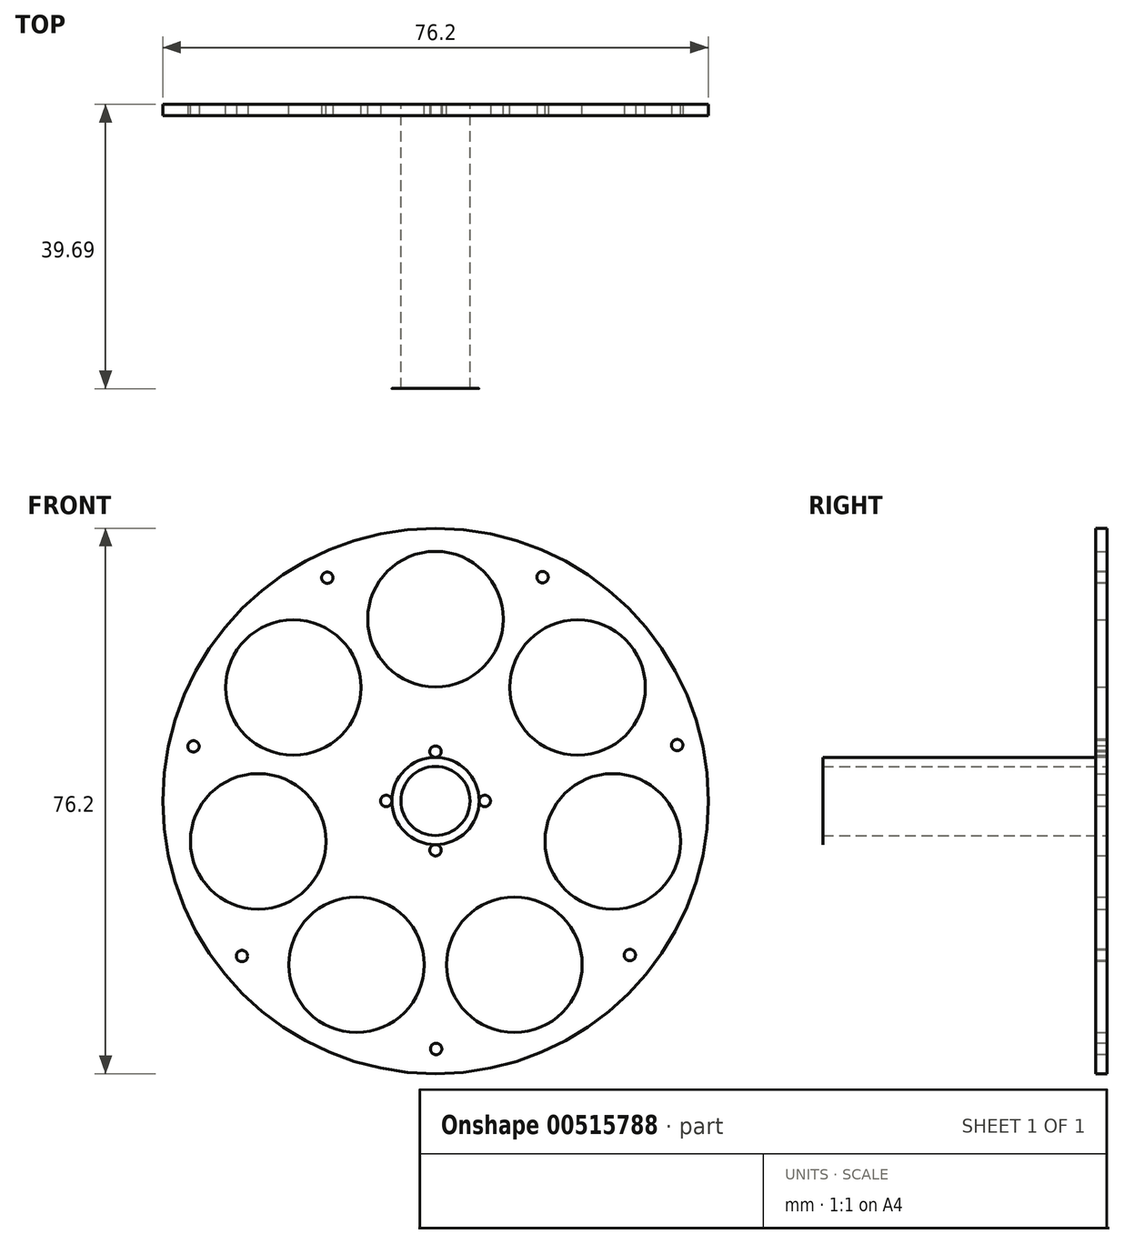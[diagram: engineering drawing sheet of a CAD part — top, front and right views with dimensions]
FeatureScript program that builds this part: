
annotation { "Feature Type Name" : "Feature", "Feature Type Description" : "" }
export const myFeature = defineFeature(function(context is Context, id is Id, definition is map)
    precondition{}
    {
        {
            var Q0;
            Q0=qCreatedBy(makeId("Front.planeOp"),FACE);
            var sketch = newSketch(context, id + "F0", { "sketchPlane" : qUnion([Q0])});
            skCircle(sketch, "E0", {"center": v(0, 0) * mm, "radius": 38.1 * mm});
            skCircle(sketch, "E1", {"center": v(0, 25.4) * mm, "radius": 9.46 * mm});
            skCircle(sketch, "E2.1.0", {"center": v(-19.86, 15.84) * mm, "radius": 9.46 * mm});
            skCircle(sketch, "E2.2.0", {"center": v(-24.76, -5.65) * mm, "radius": 9.46 * mm});
            skCircle(sketch, "E2.3.0", {"center": v(-11.02, -22.88) * mm, "radius": 9.46 * mm});
            skCircle(sketch, "E2.4.0", {"center": v(11.02, -22.88) * mm, "radius": 9.46 * mm});
            skCircle(sketch, "E2.5.0", {"center": v(24.76, -5.65) * mm, "radius": 9.46 * mm});
            skCircle(sketch, "E2.6.0", {"center": v(19.86, 15.84) * mm, "radius": 9.46 * mm});
            skCircle(sketch, "E3", {"center": v(0, 0) * mm, "radius": 4.83 * mm});
            skSolve(sketch);
        }
        {
            var Q0;
            Q0=makeQuery(id+"F0.imprint","IMPRINT",FACE,{"disambiguationData":[TD([[makeQuery(id+"F0.imprint","IMPRINT",EDGE,{"derivedFrom":sQuery(id+"F0.wireOp",EDGE,"E0")}),1.0]])]});
            extrude(context, id + "F1", {"entities" : qUnion([Q0]), "depth" : 1.59 * mm, "offsetDistance" : 25.4 * mm});
        }
        {
            var Q0;
            Q0=makeQuery(id+"F1.opExtrude","CAP_FACE",FACE,{"disambiguationData":[OSD([sQuery(id+"F0.wireOp",EDGE,"E0"),sQuery(id+"F0.wireOp",EDGE,"E1"),sQuery(id+"F0.wireOp",EDGE,"E2.1.0"),sQuery(id+"F0.wireOp",EDGE,"E2.2.0"),sQuery(id+"F0.wireOp",EDGE,"E2.3.0"),sQuery(id+"F0.wireOp",EDGE,"E2.4.0"),sQuery(id+"F0.wireOp",EDGE,"E2.5.0"),sQuery(id+"F0.wireOp",EDGE,"E2.6.0"),sQuery(id+"F0.wireOp",EDGE,"E3")])],"isStart":false});
            var sketch = newSketch(context, id + "F2", { "sketchPlane" : qUnion([Q0])});
            skCircle(sketch, "E4", {"center": v(0, 0) * mm, "radius": 4.83 * mm});
            skCircle(sketch, "E5", {"center": v(0, 0) * mm, "radius": 6.1 * mm});
            skSolve(sketch);
        }
        {
            var Q0;
            Q0=makeQuery(id+"F2.imprint","IMPRINT",FACE,{"disambiguationData":[TD([[makeQuery(id+"F2.imprint","IMPRINT",EDGE,{"derivedFrom":sQuery(id+"F2.wireOp",EDGE,"E4")}),-1.0]])]});
            extrude(context, id + "F3", {"entities" : qUnion([Q0]), "operationType" : NewBodyOperationType.ADD, "depth" : 38.1 * mm, "offsetDistance" : 25.4 * mm});
        }
        {
            var Q0;
            Q0=makeQuery(id+"F1.opExtrude","CAP_FACE",FACE,{"disambiguationData":[OSD([sQuery(id+"F0.wireOp",EDGE,"E0"),sQuery(id+"F0.wireOp",EDGE,"E1"),sQuery(id+"F0.wireOp",EDGE,"E2.1.0"),sQuery(id+"F0.wireOp",EDGE,"E2.2.0"),sQuery(id+"F0.wireOp",EDGE,"E2.3.0"),sQuery(id+"F0.wireOp",EDGE,"E2.4.0"),sQuery(id+"F0.wireOp",EDGE,"E2.5.0"),sQuery(id+"F0.wireOp",EDGE,"E2.6.0"),sQuery(id+"F0.wireOp",EDGE,"E3")])],"isStart":false});
            var sketch = newSketch(context, id + "F4", { "sketchPlane" : qUnion([Q0])});
            skCircle(sketch, "E6", {"center": v(6.89, 0) * mm, "radius": 0.8 * mm});
            skCircle(sketch, "E7.1.0", {"center": v(0, 6.89) * mm, "radius": 0.8 * mm});
            skCircle(sketch, "E7.2.0", {"center": v(-6.89, 0) * mm, "radius": 0.8 * mm});
            skCircle(sketch, "E7.3.0", {"center": v(0, -6.89) * mm, "radius": 0.8 * mm});
            skPoint(sketch, "E7.center", {"position": v(0, 0) * mm});
            skCircle(sketch, "E8", {"center": v(33.76, 7.8) * mm, "radius": 0.8 * mm});
            skCircle(sketch, "E9.1.0", {"center": v(14.95, 31.26) * mm, "radius": 0.8 * mm});
            skCircle(sketch, "E9.2.0", {"center": v(-15.12, 31.18) * mm, "radius": 0.8 * mm});
            skCircle(sketch, "E9.3.0", {"center": v(-33.8, 7.62) * mm, "radius": 0.8 * mm});
            skCircle(sketch, "E9.4.0", {"center": v(-27.03, -21.67) * mm, "radius": 0.8 * mm});
            skCircle(sketch, "E9.5.0", {"center": v(0.09, -34.65) * mm, "radius": 0.8 * mm});
            skCircle(sketch, "E9.6.0", {"center": v(27.15, -21.53) * mm, "radius": 0.8 * mm});
            skSolve(sketch);
        }
        {
            var Q0;
            Q0=makeQuery(id+"F4.imprint","IMPRINT",FACE,{"disambiguationData":[TD([[makeQuery(id+"F4.imprint","IMPRINT",EDGE,{"derivedFrom":sQuery(id+"F4.wireOp",EDGE,"E7.3.0")}),1.0]])]});
            var Q1;
            Q1=makeQuery(id+"F4.imprint","IMPRINT",FACE,{"disambiguationData":[TD([[makeQuery(id+"F4.imprint","IMPRINT",EDGE,{"derivedFrom":sQuery(id+"F4.wireOp",EDGE,"E6")}),1.0]])]});
            var Q2;
            Q2=makeQuery(id+"F4.imprint","IMPRINT",FACE,{"disambiguationData":[TD([[makeQuery(id+"F4.imprint","IMPRINT",EDGE,{"derivedFrom":sQuery(id+"F4.wireOp",EDGE,"E9.6.0")}),1.0]])]});
            var Q3;
            Q3=makeQuery(id+"F4.imprint","IMPRINT",FACE,{"disambiguationData":[TD([[makeQuery(id+"F4.imprint","IMPRINT",EDGE,{"derivedFrom":sQuery(id+"F4.wireOp",EDGE,"E8")}),1.0]])]});
            var Q4;
            Q4=makeQuery(id+"F4.imprint","IMPRINT",FACE,{"disambiguationData":[TD([[makeQuery(id+"F4.imprint","IMPRINT",EDGE,{"derivedFrom":sQuery(id+"F4.wireOp",EDGE,"E9.5.0")}),1.0]])]});
            var Q5;
            Q5=makeQuery(id+"F4.imprint","IMPRINT",FACE,{"disambiguationData":[TD([[makeQuery(id+"F4.imprint","IMPRINT",EDGE,{"derivedFrom":sQuery(id+"F4.wireOp",EDGE,"E9.4.0")}),1.0]])]});
            var Q6;
            Q6=makeQuery(id+"F4.imprint","IMPRINT",FACE,{"disambiguationData":[TD([[makeQuery(id+"F4.imprint","IMPRINT",EDGE,{"derivedFrom":sQuery(id+"F4.wireOp",EDGE,"E9.3.0")}),1.0]])]});
            var Q7;
            Q7=makeQuery(id+"F4.imprint","IMPRINT",FACE,{"disambiguationData":[TD([[makeQuery(id+"F4.imprint","IMPRINT",EDGE,{"derivedFrom":sQuery(id+"F4.wireOp",EDGE,"E9.2.0")}),1.0]])]});
            var Q8;
            Q8=makeQuery(id+"F4.imprint","IMPRINT",FACE,{"disambiguationData":[TD([[makeQuery(id+"F4.imprint","IMPRINT",EDGE,{"derivedFrom":sQuery(id+"F4.wireOp",EDGE,"E9.1.0")}),1.0]])]});
            var Q9;
            Q9=makeQuery(id+"F4.imprint","IMPRINT",FACE,{"disambiguationData":[TD([[makeQuery(id+"F4.imprint","IMPRINT",EDGE,{"derivedFrom":sQuery(id+"F4.wireOp",EDGE,"E7.1.0")}),1.0]])]});
            var Q10;
            Q10=makeQuery(id+"F4.imprint","IMPRINT",FACE,{"disambiguationData":[TD([[makeQuery(id+"F4.imprint","IMPRINT",EDGE,{"derivedFrom":sQuery(id+"F4.wireOp",EDGE,"E7.2.0")}),1.0]])]});
            extrude(context, id + "F5", {"entities" : qUnion([Q0, Q1, Q2, Q3, Q4, Q5, Q6, Q7, Q8, Q9, Q10]), "operationType" : NewBodyOperationType.REMOVE, "oppositeDirection" : true, "depth" : 282.45 * mm, "offsetDistance" : 25.4 * mm});
        }
    });
